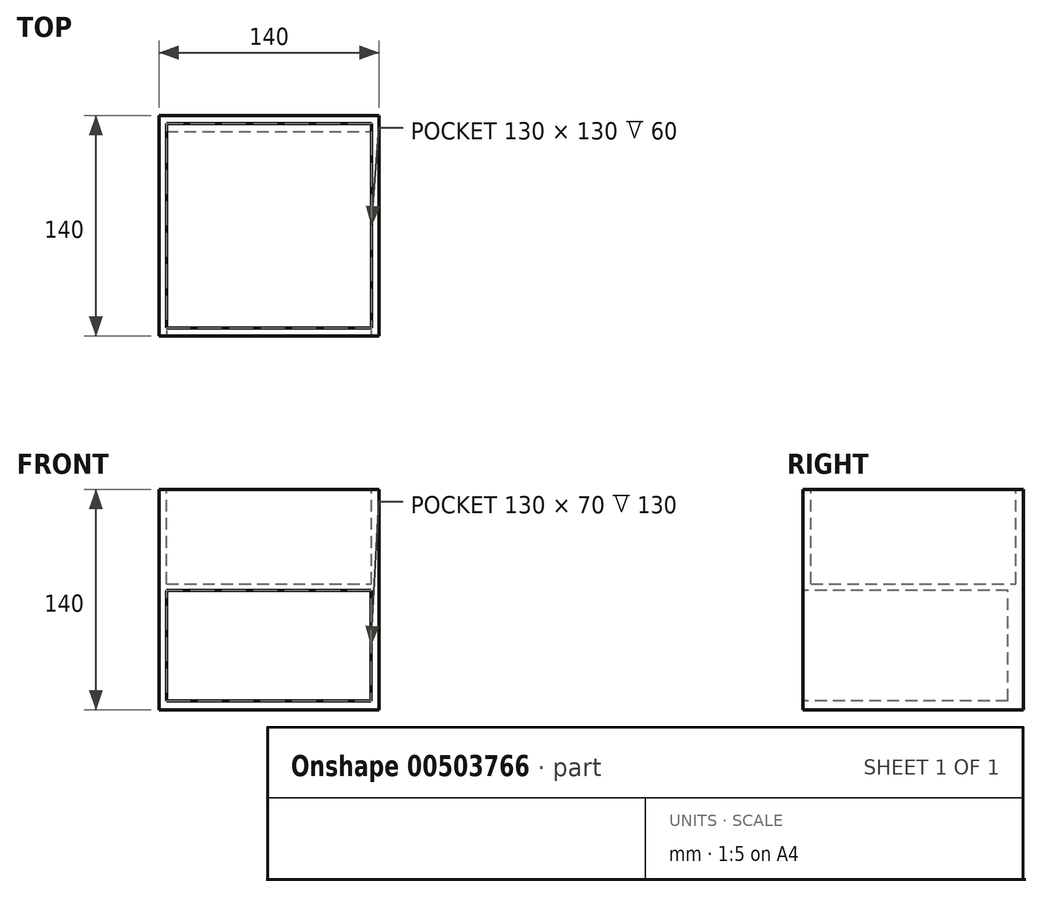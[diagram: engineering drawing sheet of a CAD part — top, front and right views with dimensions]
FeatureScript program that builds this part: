
annotation { "Feature Type Name" : "Feature", "Feature Type Description" : "" }
export const myFeature = defineFeature(function(context is Context, id is Id, definition is map)
    precondition{}
    {
        {
            var Q0;
            Q0=qCreatedBy(makeId("Top.planeOp"),FACE);
            var sketch = newSketch(context, id + "F0", { "sketchPlane" : qUnion([Q0])});
            skLineSegment(sketch, "E0.bottom", {"start": v(-70, -70) * mm, "end": v(70, -70) * mm});
            skLineSegment(sketch, "E0.top", {"start": v(-70, 70) * mm, "end": v(70, 70) * mm});
            skLineSegment(sketch, "E0.left", {"start": v(-70, -70) * mm, "end": v(-70, 70) * mm});
            skLineSegment(sketch, "E0.right", {"start": v(70, -70) * mm, "end": v(70, 70) * mm});
            skPoint(sketch, "E0.middle", {"position": v(0, 0) * mm});
            skSolve(sketch);
        }
        {
            var Q0;
            Q0=makeQuery(id+"F0.imprint","IMPRINT",FACE,{"disambiguationData":[TD([[makeQuery(id+"F0.imprint","IMPRINT",EDGE,{"derivedFrom":sQuery(id+"F0.wireOp",EDGE,"E0.bottom")}),1.0]])]});
            extrude(context, id + "F1", {"entities" : qUnion([Q0]), "depth" : 140 * mm});
        }
        {
            var Q0;
            Q0=makeQuery(id+"F1.opExtrude","CAP_FACE",FACE,{"disambiguationData":[OSD([sQuery(id+"F0.wireOp",EDGE,"E0.bottom"),sQuery(id+"F0.wireOp",EDGE,"E0.top"),sQuery(id+"F0.wireOp",EDGE,"E0.left"),sQuery(id+"F0.wireOp",EDGE,"E0.right")])],"isStart":false});
            var sketch = newSketch(context, id + "F2", { "sketchPlane" : qUnion([Q0])});
            skLineSegment(sketch, "E1.0", {"start": v(-65, 65) * mm, "end": v(65, 65) * mm});
            skLineSegment(sketch, "E1.1", {"start": v(-65, -65) * mm, "end": v(-65, 65) * mm});
            skLineSegment(sketch, "E1.2", {"start": v(-65, -65) * mm, "end": v(65, -65) * mm});
            skLineSegment(sketch, "E1.3", {"start": v(65, -65) * mm, "end": v(65, 65) * mm});
            skSolve(sketch);
        }
        {
            var Q0;
            Q0=makeQuery(id+"F2.imprint","IMPRINT",FACE,{"disambiguationData":[TD([[makeQuery(id+"F2.imprint","IMPRINT",EDGE,{"derivedFrom":sQuery(id+"F2.wireOp",EDGE,"E1.0")}),-1.0]])]});
            extrude(context, id + "F3", {"entities" : qUnion([Q0]), "operationType" : NewBodyOperationType.REMOVE, "oppositeDirection" : true, "depth" : 60 * mm});
        }
        {
            var Q0;
            Q0=makeQuery(id+"F1.opExtrude","SWEPT_FACE",FACE,{"disambiguationData":[OSD([sQuery(id+"F0.wireOp",EDGE,"E0.bottom")])]});
            var sketch = newSketch(context, id + "F4", { "sketchPlane" : qUnion([Q0])});
            skLineSegment(sketch, "E2.bottom", {"start": v(-65.2, 5.87) * mm, "end": v(64.8, 5.87) * mm});
            skLineSegment(sketch, "E2.top", {"start": v(-65.2, 75.87) * mm, "end": v(64.8, 75.87) * mm});
            skLineSegment(sketch, "E2.left", {"start": v(-65.2, 5.87) * mm, "end": v(-65.2, 75.87) * mm});
            skLineSegment(sketch, "E2.right", {"start": v(64.8, 5.87) * mm, "end": v(64.8, 75.87) * mm});
            skSolve(sketch);
        }
        {
            var Q0;
            Q0=makeQuery(id+"F4.imprint","IMPRINT",FACE,{"disambiguationData":[TD([[makeQuery(id+"F4.imprint","IMPRINT",EDGE,{"derivedFrom":sQuery(id+"F4.wireOp",EDGE,"E2.bottom")}),1.0]])]});
            extrude(context, id + "F5", {"entities" : qUnion([Q0]), "operationType" : NewBodyOperationType.REMOVE, "oppositeDirection" : true, "depth" : 130 * mm});
        }
    });
